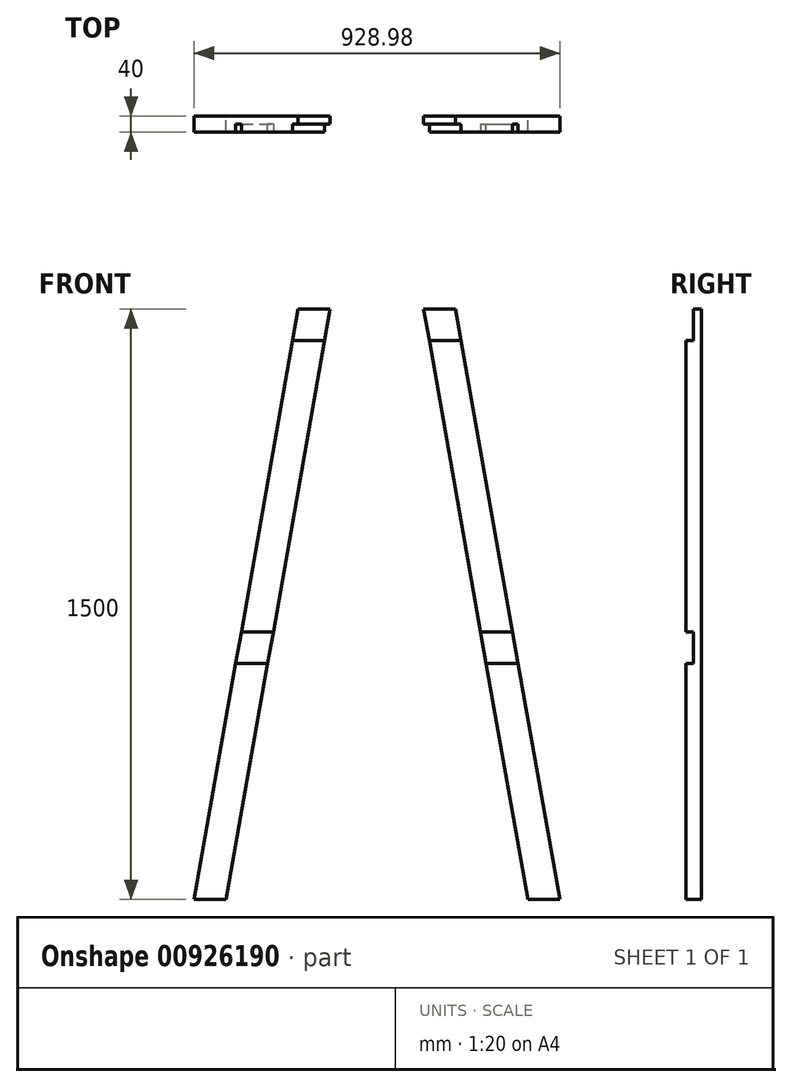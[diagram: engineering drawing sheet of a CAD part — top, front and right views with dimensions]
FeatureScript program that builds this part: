
annotation { "Feature Type Name" : "Feature", "Feature Type Description" : "" }
export const myFeature = defineFeature(function(context is Context, id is Id, definition is map)
    precondition{}
    {
        {
            var Q0;
            Q0=qCreatedBy(makeId("Front.planeOp"),FACE);
            var sketch = newSketch(context, id + "F0", { "sketchPlane" : qUnion([Q0])});
            skLineSegment(sketch, "E0", {"start": v(-200, 1500) * mm, "end": v(-464.5, 0) * mm, "construction": true});
            skLineSegment(sketch, "E1", {"start": v(-464.5, 0) * mm, "end": v(464.5, 0) * mm, "construction": true});
            skLineSegment(sketch, "E2", {"start": v(464.5, 0) * mm, "end": v(200, 1500) * mm, "construction": true});
            skLineSegment(sketch, "E3", {"start": v(200, 1500) * mm, "end": v(-200, 1500) * mm, "construction": true});
            skSolve(sketch);
        }
        {
            var Q0;
            Q0=qCreatedBy(makeId("Front.planeOp"),FACE);
            var sketch = newSketch(context, id + "F1", { "sketchPlane" : qUnion([Q0])});
            skLineSegment(sketch, "E4", {"start": v(-200, 1500) * mm, "end": v(-118.77, 1500) * mm});
            skLineSegment(sketch, "E5", {"start": v(-118.77, 1500) * mm, "end": v(-383.26, 0) * mm});
            skLineSegment(sketch, "E6", {"start": v(-383.26, 0) * mm, "end": v(-464.5, 0) * mm});
            skLineSegment(sketch, "E7", {"start": v(-464.5, 0) * mm, "end": v(-200, 1500) * mm});
            skLineSegment(sketch, "E8", {"start": v(0, 1685.12) * mm, "end": v(0, -287.57) * mm, "construction": true});
            skLineSegment(sketch, "E9.MirrorCS", {"start": v(383.26, 0) * mm, "end": v(464.5, 0) * mm});
            skLineSegment(sketch, "E10.MirrorCS", {"start": v(200, 1500) * mm, "end": v(118.77, 1500) * mm});
            skLineSegment(sketch, "E11.MirrorCS", {"start": v(118.77, 1500) * mm, "end": v(383.26, 0) * mm});
            skLineSegment(sketch, "E12.MirrorCS", {"start": v(464.5, 0) * mm, "end": v(200, 1500) * mm});
            skLineSegment(sketch, "E13", {"start": v(-383.26, 0) * mm, "end": v(-462.04, 13.9) * mm, "construction": true});
            skLineSegment(sketch, "E14", {"start": v(383.26, 0) * mm, "end": v(462.04, 13.9) * mm, "construction": true});
            skSolve(sketch);
        }
        {
            var Q0;
            Q0 = qSketchRegion(id + "F1", true);
            extrude(context, id + "F2", {"entities" : qUnion([Q0]), "depth" : 40 * mm, "offsetDistance" : 25 * mm});
        }
        {
            var Q0;
            Q0=makeQuery(id+"F2.opExtrude","CAP_FACE",FACE,{"disambiguationData":[OSD([sQuery(id+"F1.wireOp",EDGE,"E4"),sQuery(id+"F1.wireOp",EDGE,"E5"),sQuery(id+"F1.wireOp",EDGE,"E6"),sQuery(id+"F1.wireOp",EDGE,"E7")])],"isStart":false});
            var sketch = newSketch(context, id + "F3", { "sketchPlane" : qUnion([Q0])});
            skLineSegment(sketch, "E15", {"start": v(-200, 1500) * mm, "end": v(-118.77, 1500) * mm});
            skLineSegment(sketch, "E16", {"start": v(-118.77, 1500) * mm, "end": v(-132.87, 1420) * mm});
            skLineSegment(sketch, "E17", {"start": v(-132.87, 1420) * mm, "end": v(-214.1, 1420) * mm});
            skLineSegment(sketch, "E18", {"start": v(-214.1, 1420) * mm, "end": v(-200, 1500) * mm});
            skLineSegment(sketch, "E19", {"start": v(-200, 1500) * mm, "end": v(-200, 1420) * mm, "construction": true});
            skLineSegment(sketch, "E20.bottom", {"start": v(-358.7, 680) * mm, "end": v(-263.35, 680) * mm});
            skLineSegment(sketch, "E20.top", {"start": v(-358.7, 600) * mm, "end": v(-263.35, 600) * mm});
            skLineSegment(sketch, "E20.left", {"start": v(-358.7, 680) * mm, "end": v(-358.7, 600) * mm});
            skLineSegment(sketch, "E20.right", {"start": v(-263.35, 680) * mm, "end": v(-263.35, 600) * mm});
            skSolve(sketch);
        }
        {
            var Q0;
            Q0 = qSketchRegion(id + "F3", true);
            extrude(context, id + "F4", {"entities" : qUnion([Q0]), "operationType" : NewBodyOperationType.REMOVE, "oppositeDirection" : true, "depth" : 20 * mm, "offsetDistance" : 25 * mm});
        }
        {
            var Q0;
            Q0 = qSketchRegion(id + "F3", true);
            extrude(context, id + "F5", {"entities" : qUnion([Q0]), "operationType" : NewBodyOperationType.REMOVE, "oppositeDirection" : true, "depth" : 20 * mm, "offsetDistance" : 25 * mm});
        }
        {
            var Q0;
            Q0=makeQuery(id+"F2.opExtrude","CAP_FACE",FACE,{"disambiguationData":[OSD([sQuery(id+"F1.wireOp",EDGE,"E9.MirrorCS"),sQuery(id+"F1.wireOp",EDGE,"E10.MirrorCS"),sQuery(id+"F1.wireOp",EDGE,"E11.MirrorCS"),sQuery(id+"F1.wireOp",EDGE,"E12.MirrorCS")])],"isStart":false});
            var sketch = newSketch(context, id + "F6", { "sketchPlane" : qUnion([Q0])});
            skLineSegment(sketch, "E21.bottom", {"start": v(118.77, 1500) * mm, "end": v(214.1, 1500) * mm});
            skLineSegment(sketch, "E21.top", {"start": v(118.77, 1420) * mm, "end": v(214.1, 1420) * mm});
            skLineSegment(sketch, "E21.left", {"start": v(118.77, 1500) * mm, "end": v(118.77, 1420) * mm});
            skLineSegment(sketch, "E21.right", {"start": v(214.1, 1500) * mm, "end": v(214.1, 1420) * mm});
            skLineSegment(sketch, "E22.bottom", {"start": v(263.35, 680) * mm, "end": v(358.7, 680) * mm});
            skLineSegment(sketch, "E22.top", {"start": v(263.35, 600) * mm, "end": v(358.7, 600) * mm});
            skLineSegment(sketch, "E22.left", {"start": v(263.35, 680) * mm, "end": v(263.35, 600) * mm});
            skLineSegment(sketch, "E22.right", {"start": v(358.7, 680) * mm, "end": v(358.7, 600) * mm});
            skSolve(sketch);
        }
        {
            var Q0;
            Q0 = qSketchRegion(id + "F6", true);
            extrude(context, id + "F7", {"entities" : qUnion([Q0]), "operationType" : NewBodyOperationType.REMOVE, "oppositeDirection" : true, "depth" : 20 * mm, "offsetDistance" : 25 * mm});
        }
    });
